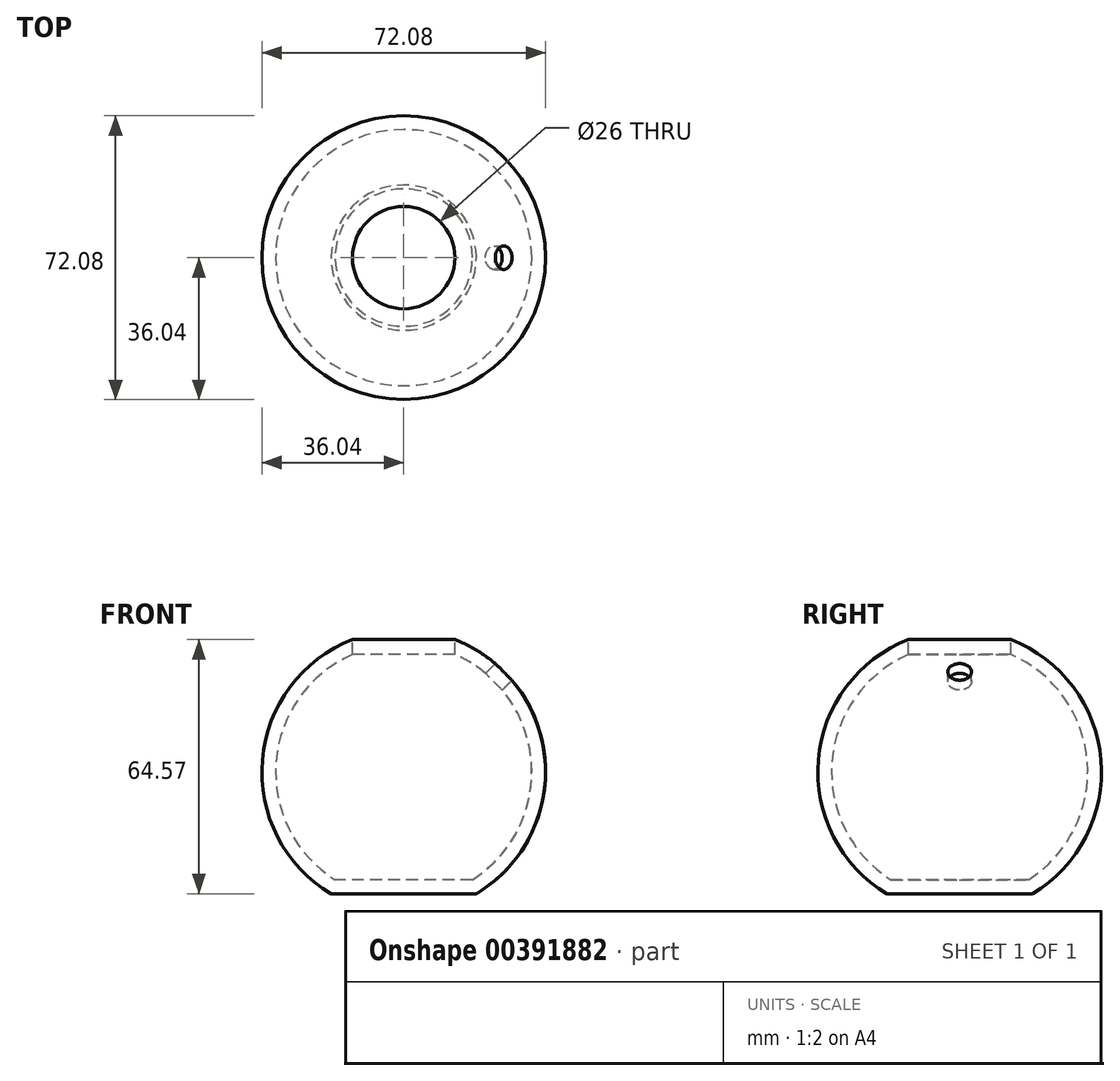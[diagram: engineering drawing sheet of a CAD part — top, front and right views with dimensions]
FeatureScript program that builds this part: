
annotation { "Feature Type Name" : "Feature", "Feature Type Description" : "" }
export const myFeature = defineFeature(function(context is Context, id is Id, definition is map)
    precondition{}
    {
        {
            var Q0;
            Q0=qCreatedBy(makeId("Right.planeOp"),FACE);
            var sketch = newSketch(context, id + "F0", { "sketchPlane" : qUnion([Q0])});
            skLineSegment(sketch, "E0", {"start": v(0, 0) * mm, "end": v(133.4, 0) * mm, "construction": true});
            skLineSegment(sketch, "E1", {"start": v(0, 0) * mm, "end": v(99.83, 99.83) * mm, "construction": true});
            skLineSegment(sketch, "E2", {"start": v(0, 0) * mm, "end": v(-89.93, 89.93) * mm, "construction": true});
            skLineSegment(sketch, "E3", {"start": v(0, 0) * mm, "end": v(-92.34, 0) * mm, "construction": true});
            skLineSegment(sketch, "E4", {"start": v(0, 0) * mm, "end": v(0, 113.78) * mm, "construction": true});
            skLineSegment(sketch, "E5", {"start": v(63.5, 63.5) * mm, "end": v(63.5, 3.5) * mm, "construction": true});
            skLineSegment(sketch, "E6", {"start": v(63.5, 0) * mm, "end": v(73.5, 0) * mm});
            skLineSegment(sketch, "E7.MirrorCS", {"start": v(63.5, 0) * mm, "end": v(53.5, 0) * mm});
            skCircle(sketch, "E8", {"center": v(63.5, 30.96) * mm, "radius": 32.54 * mm});
            skLineSegment(sketch, "E9", {"start": v(63.5, 3.5) * mm, "end": v(63.5, 3.5) * mm});
            skLineSegment(sketch, "E10.MirrorCS", {"start": v(63.5, 3.5) * mm, "end": v(46.05, 3.5) * mm});
            skLineSegment(sketch, "E11", {"start": v(53.5, 0) * mm, "end": v(45.06, 0) * mm});
            skLineSegment(sketch, "E12", {"start": v(73.5, 0) * mm, "end": v(81.94, 0) * mm});
            skLineSegment(sketch, "E13", {"start": v(63.5, 60.8) * mm, "end": v(76.5, 60.8) * mm, "construction": true});
            skLineSegment(sketch, "E14.MirrorCS", {"start": v(63.5, 60.8) * mm, "end": v(50.5, 60.8) * mm, "construction": true});
            skLineSegment(sketch, "E15", {"start": v(76.5, 60.8) * mm, "end": v(76.5, 64.57) * mm});
            skLineSegment(sketch, "E16.MirrorCS", {"start": v(50.5, 60.8) * mm, "end": v(50.5, 64.57) * mm});
            skLineSegment(sketch, "E17", {"start": v(80.95, 3.5) * mm, "end": v(86.83, 3.5) * mm, "construction": true});
            skLineSegment(sketch, "E18", {"start": v(46.05, 3.5) * mm, "end": v(40.17, 3.5) * mm, "construction": true});
            skLineSegment(sketch, "E19", {"start": v(63.5, 3.5) * mm, "end": v(80.95, 3.5) * mm});
            skLineSegment(sketch, "E20", {"start": v(63.5, 3.5) * mm, "end": v(63.5, 0) * mm});
            skLineSegment(sketch, "E21", {"start": v(45.06, 0) * mm, "end": v(-54.94, 0) * mm});
            skLineSegment(sketch, "E22", {"start": v(41.06, 59.16) * mm, "end": v(41.06, 59.16) * mm});
            skLineSegment(sketch, "E23", {"start": v(-54.94, 59.16) * mm, "end": v(-54.94, 0) * mm});
            skLineSegment(sketch, "E24", {"start": v(41.06, 59.16) * mm, "end": v(-54.94, 59.16) * mm});
            skArc(sketch, "E25", {"start": v(41.06, 59.16) * mm, "mid": v(27.54, 28.53) * mm, "end": v(45.06, 0) * mm});
            skArc(sketch, "E26", {"start": v(45.06, 0) * mm, "mid": v(99.46, 33.4) * mm, "end": v(41.06, 59.16) * mm});
            skArc(sketch, "E27.0", {"start": v(33.9, 56.26) * mm, "mid": v(24.6, 29.06) * mm, "end": v(36.5, 2.9) * mm});
            skLineSegment(sketch, "E27.1", {"start": v(33.9, 56.26) * mm, "end": v(-52.04, 56.26) * mm});
            skLineSegment(sketch, "E27.2", {"start": v(-52.04, 56.26) * mm, "end": v(-52.04, 2.9) * mm});
            skLineSegment(sketch, "E27.3", {"start": v(36.5, 2.9) * mm, "end": v(-52.04, 2.9) * mm});
            skFitSpline(sketch, "E28", {"points": [v(46.15, 51.65) * mm, v(46.5, 7.66) * mm, v(28.87, 5.74) * mm, v(21.53, 28.95) * mm, v(24.07, 44.97) * mm, v(23.45, 53.04) * mm, v(17.5, 47.75) * mm, v(17.35, 13.25) * mm, v(10.92, 42.93) * mm, v(6.68, 52.58) * mm, v(3.46, 36.2) * mm, v(-2.55, 51.65) * mm, v(-7.8, 52.52) * mm, v(-5.31, 16.46) * mm, v(-9.36, 6.44) * mm, v(-48.11, 6.44) * mm, v(-47.59, 11.15) * mm, v(-11.1, 13.94) * mm, v(-12.15, 20.05) * mm, v(-46.54, 17.6) * mm, v(-47.41, 24.24) * mm, v(-12.5, 25.99) * mm, v(-13.55, 32.97) * mm, v(-47.41, 32.1) * mm, v(-47.41, 38.38) * mm, v(-14.42, 42.22) * mm, v(-19.83, 52.52) * mm, v(-34.32, 45.54) * mm, v(-69.06, 52.17) * mm], "startDerivative": vector(218.64, -1158.44) * mm, "endDerivative": vector(-919.51, 353.19) * mm});
            skSolve(sketch);
        }
        {
            var Q0;
            {var subQ0=sQuery(id+"F0.wireOp",EDGE,"E6");Q0=makeQuery(id+"F0.imprint","IMPRINT",FACE,{"disambiguationData":[TD([[makeQuery(id+"F0.imprint","IMPRINT",EDGE,{"derivedFrom":subQ0}),1.0]])]});}
            var Q1;
            {var subQ0=sQuery(id+"F0.wireOp",EDGE,"E12");Q1=makeQuery(id+"F0.imprint","IMPRINT",FACE,{"disambiguationData":[TD([[makeQuery(id+"F0.imprint","IMPRINT",EDGE,{"derivedFrom":subQ0}),1.0]])]});}
            var Q2;
            Q2=sQuery(id+"F0.wireOp",EDGE,"E5");
            revolve(context, id + "F1", {"entities" : qUnion([Q0, Q1]), "axis" : qUnion([Q2]), "revolveType" : RevolveType.FULL});
        }
        {
            var Q0;
            Q0=sQuery(id+"F0.wireOp",EDGE,"E5");
            cPlane(context, id + "F2", {"entities" : qUnion([Q0]), "cplaneType" : CPlaneType.LINE_ANGLE, "offset" : 25 * mm, "angle" : 90 * degree, "width" : 150 * mm, "height" : 150 * mm});
        }
        {
            var Q0;
            Q0=qCreatedBy(id+"F2.planeOp",FACE);
            var sketch = newSketch(context, id + "F3", { "sketchPlane" : qUnion([Q0])});
            skPoint(sketch, "E29.0", {"position": v(0, 30.96) * mm});
            skLineSegment(sketch, "E30", {"start": v(0, 30.96) * mm, "end": v(-30.56, 61.52) * mm, "construction": true});
            skLineSegment(sketch, "E31", {"start": v(0, 30.96) * mm, "end": v(0, 61.52) * mm, "construction": true});
            skLineSegment(sketch, "E32", {"start": v(-21.23, 52.2) * mm, "end": v(-19.11, 54.32) * mm});
            skLineSegment(sketch, "E33", {"start": v(-19.11, 54.32) * mm, "end": v(-25.25, 60.45) * mm});
            skLineSegment(sketch, "E34", {"start": v(-25.25, 60.45) * mm, "end": v(-27.37, 58.33) * mm});
            skLineSegment(sketch, "E35", {"start": v(-27.37, 58.33) * mm, "end": v(-21.23, 52.2) * mm});
            skSolve(sketch);
        }
        {
            var Q0;
            Q0=makeQuery(id+"F3.imprint","IMPRINT",FACE,{"disambiguationData":[TD([[makeQuery(id+"F3.imprint","IMPRINT",EDGE,{"derivedFrom":sQuery(id+"F3.wireOp",EDGE,"E32")}),1.0]])]});
            var Q1;
            Q1=sQuery(id+"F3.wireOp",EDGE,"E30");
            revolve(context, id + "F4", {"operationType" : NewBodyOperationType.REMOVE, "entities" : qUnion([Q0]), "axis" : qUnion([Q1]), "revolveType" : RevolveType.FULL, "oppositeDirection" : true});
        }
        {
            var Q0;
            Q0=sQuery(id+"F0.wireOp",VERTEX,"E28.0.internal");
            var Q1;
            Q1=qCreatedBy(makeId("Top.planeOp"),FACE);
            cPlane(context, id + "F5", {"entities" : qUnion([Q0, Q1]), "cplaneType" : CPlaneType.PLANE_POINT, "offset" : 25 * mm, "width" : 150 * mm, "height" : 150 * mm});
        }
    });
